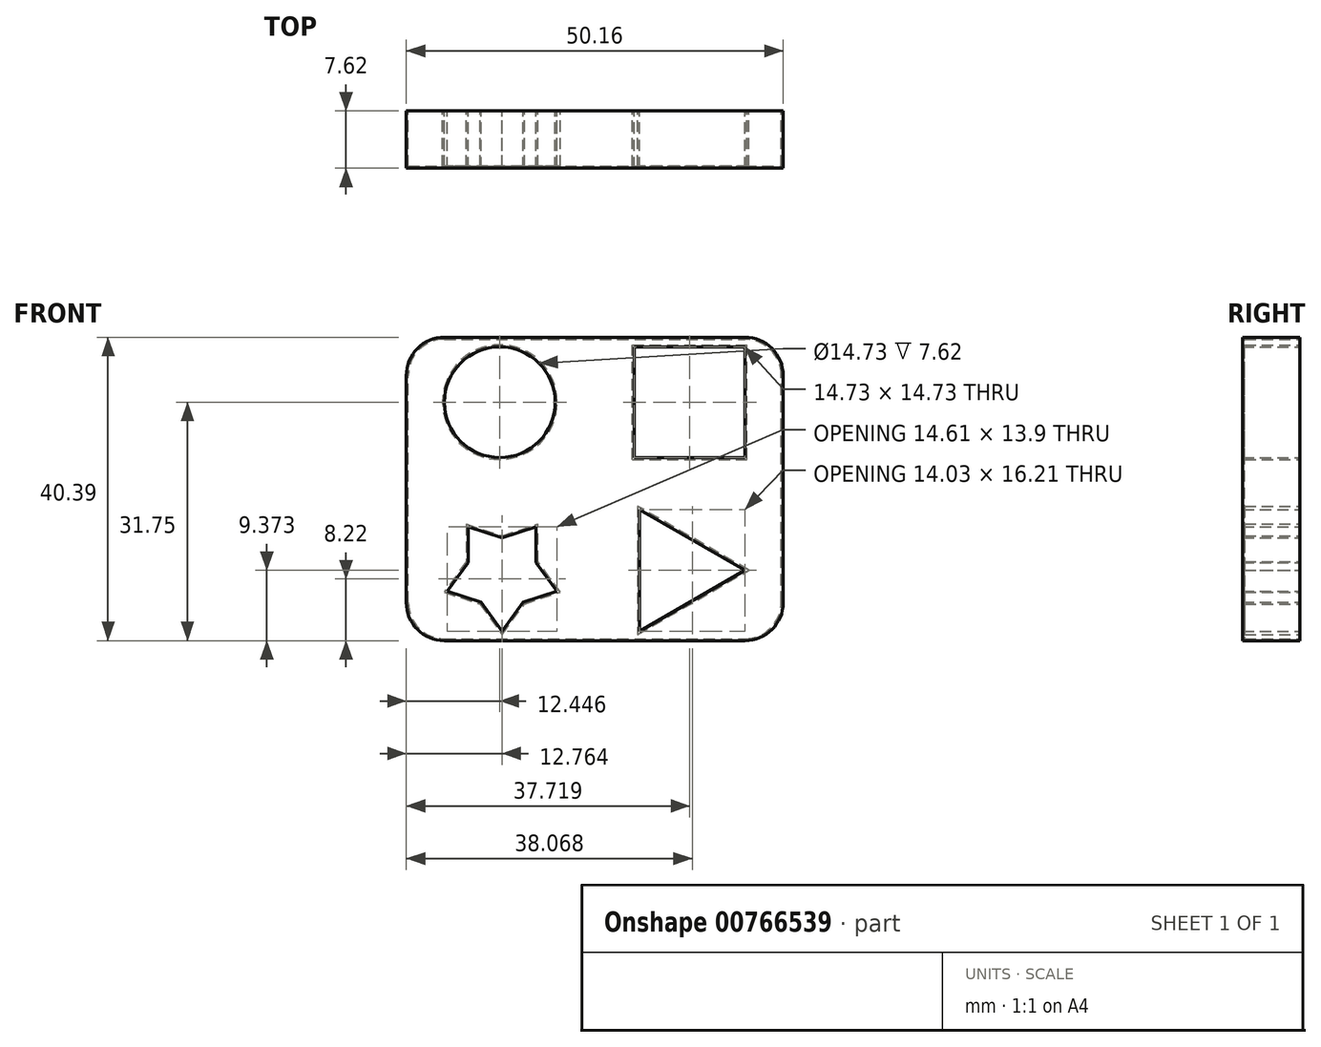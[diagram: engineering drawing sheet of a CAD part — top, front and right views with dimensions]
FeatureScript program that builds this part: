
annotation { "Feature Type Name" : "Feature", "Feature Type Description" : "" }
export const myFeature = defineFeature(function(context is Context, id is Id, definition is map)
    precondition{}
    {
        {
            var Q0;
            Q0=qCreatedBy(makeId("Front.planeOp"),FACE);
            var sketch = newSketch(context, id + "F0", { "sketchPlane" : qUnion([Q0])});
            skLineSegment(sketch, "E0.bottom", {"start": v(5.08, 0) * mm, "end": v(45.08, 0) * mm});
            skLineSegment(sketch, "E0.top", {"start": v(5.08, 40.39) * mm, "end": v(45.09, 40.39) * mm});
            skLineSegment(sketch, "E0.left", {"start": v(0, 5.08) * mm, "end": v(0, 35.3) * mm});
            skLineSegment(sketch, "E0.right", {"start": v(50.16, 5.08) * mm, "end": v(50.16, 35.3) * mm});
            skPoint(sketch, "E1.visualSharp", {"position": v(0, 40.39) * mm});
            skArc(sketch, "E1.filletArc", {"start": v(5.08, 40.39) * mm, "mid": v(1.49, 38.9) * mm, "end": v(0, 35.3) * mm});
            skPoint(sketch, "E2.visualSharp", {"position": v(0, 0) * mm});
            skArc(sketch, "E2.filletArc", {"start": v(0, 5.08) * mm, "mid": v(1.49, 1.49) * mm, "end": v(5.08, 0) * mm});
            skPoint(sketch, "E3.visualSharp", {"position": v(50.16, 0) * mm});
            skArc(sketch, "E3.filletArc", {"start": v(45.09, 0) * mm, "mid": v(48.68, 1.49) * mm, "end": v(50.17, 5.08) * mm});
            skPoint(sketch, "E4.visualSharp", {"position": v(50.17, 40.39) * mm});
            skArc(sketch, "E4.filletArc", {"start": v(50.17, 35.3) * mm, "mid": v(48.68, 38.9) * mm, "end": v(45.09, 40.39) * mm});
            skLineSegment(sketch, "E5.bottom", {"start": v(30.35, 24.38) * mm, "end": v(45.09, 24.38) * mm});
            skLineSegment(sketch, "E5.top", {"start": v(30.35, 39.12) * mm, "end": v(45.09, 39.12) * mm});
            skLineSegment(sketch, "E5.left", {"start": v(30.35, 24.38) * mm, "end": v(30.35, 39.12) * mm});
            skLineSegment(sketch, "E5.right", {"start": v(45.08, 24.38) * mm, "end": v(45.08, 39.12) * mm});
            skCircle(sketch, "E6", {"center": v(12.45, 31.75) * mm, "radius": 7.37 * mm});
            skCircle(sketch, "E7.cCircle", {"center": v(12.76, 8.95) * mm, "radius": 7.68 * mm, "construction": true});
            skLineSegment(sketch, "E7.0", {"start": v(17.28, 15.17) * mm, "end": v(20.07, 6.58) * mm, "construction": true});
            skLineSegment(sketch, "E7.1", {"start": v(20.07, 6.58) * mm, "end": v(12.76, 1.27) * mm, "construction": true});
            skLineSegment(sketch, "E7.2", {"start": v(12.76, 1.27) * mm, "end": v(5.46, 6.58) * mm, "construction": true});
            skLineSegment(sketch, "E7.3", {"start": v(5.46, 6.58) * mm, "end": v(8.25, 15.17) * mm, "construction": true});
            skLineSegment(sketch, "E7.4", {"start": v(8.25, 15.17) * mm, "end": v(17.28, 15.17) * mm, "construction": true});
            skLineSegment(sketch, "E8", {"start": v(8.25, 15.17) * mm, "end": v(12.76, 13.7) * mm});
            skLineSegment(sketch, "E9", {"start": v(12.76, 13.7) * mm, "end": v(17.28, 15.17) * mm});
            skLineSegment(sketch, "E10", {"start": v(16.42, 3.92) * mm, "end": v(12.76, 8.95) * mm, "construction": true});
            skLineSegment(sketch, "E11", {"start": v(9.1, 3.92) * mm, "end": v(12.76, 8.95) * mm, "construction": true});
            skLineSegment(sketch, "E12", {"start": v(18.68, 10.87) * mm, "end": v(12.76, 8.95) * mm, "construction": true});
            skLineSegment(sketch, "E13", {"start": v(6.85, 10.87) * mm, "end": v(12.76, 8.95) * mm, "construction": true});
            skLineSegment(sketch, "E14", {"start": v(8.25, 15.17) * mm, "end": v(8.25, 10.42) * mm});
            skLineSegment(sketch, "E15", {"start": v(8.25, 10.42) * mm, "end": v(5.46, 6.58) * mm});
            skLineSegment(sketch, "E16", {"start": v(5.46, 6.58) * mm, "end": v(9.97, 5.11) * mm});
            skLineSegment(sketch, "E17", {"start": v(9.97, 5.11) * mm, "end": v(12.76, 1.27) * mm});
            skLineSegment(sketch, "E18", {"start": v(12.76, 1.27) * mm, "end": v(15.55, 5.11) * mm});
            skLineSegment(sketch, "E19", {"start": v(15.55, 5.11) * mm, "end": v(20.07, 6.58) * mm});
            skLineSegment(sketch, "E20", {"start": v(20.07, 6.58) * mm, "end": v(17.28, 10.42) * mm});
            skLineSegment(sketch, "E21", {"start": v(17.28, 10.42) * mm, "end": v(17.28, 15.17) * mm});
            skLineSegment(sketch, "E22", {"start": v(31.05, 17.48) * mm, "end": v(31.05, 1.27) * mm});
            skLineSegment(sketch, "E23", {"start": v(31.05, 1.27) * mm, "end": v(45.09, 9.37) * mm});
            skLineSegment(sketch, "E24", {"start": v(45.09, 9.37) * mm, "end": v(31.05, 17.48) * mm});
            skSolve(sketch);
        }
        {
            var Q0;
            Q0=makeQuery(id+"F0.imprint","IMPRINT",FACE,{"disambiguationData":[TD([[makeQuery(id+"F0.imprint","IMPRINT",EDGE,{"derivedFrom":sQuery(id+"F0.wireOp",EDGE,"E0.bottom")}),1.0]])]});
            extrude(context, id + "F1", {"entities" : qUnion([Q0]), "depth" : 7.62 * mm, "offsetDistance" : 25.4 * mm});
        }
        {
            var Q0;
            Q0=makeQuery(id+"F1.opExtrude","CAP_FACE",FACE,{"disambiguationData":[OSD([sQuery(id+"F0.wireOp",EDGE,"E0.bottom"),sQuery(id+"F0.wireOp",EDGE,"E0.top"),sQuery(id+"F0.wireOp",EDGE,"E0.left"),sQuery(id+"F0.wireOp",EDGE,"E0.right"),sQuery(id+"F0.wireOp",EDGE,"E1.filletArc"),sQuery(id+"F0.wireOp",EDGE,"E2.filletArc"),sQuery(id+"F0.wireOp",EDGE,"E3.filletArc"),sQuery(id+"F0.wireOp",EDGE,"E4.filletArc"),sQuery(id+"F0.wireOp",EDGE,"E5.bottom"),sQuery(id+"F0.wireOp",EDGE,"E5.top"),sQuery(id+"F0.wireOp",EDGE,"E5.left"),sQuery(id+"F0.wireOp",EDGE,"E5.right"),sQuery(id+"F0.wireOp",EDGE,"E6"),sQuery(id+"F0.wireOp",EDGE,"E8"),sQuery(id+"F0.wireOp",EDGE,"E9"),sQuery(id+"F0.wireOp",EDGE,"E14"),sQuery(id+"F0.wireOp",EDGE,"E15"),sQuery(id+"F0.wireOp",EDGE,"E16"),sQuery(id+"F0.wireOp",EDGE,"E17"),sQuery(id+"F0.wireOp",EDGE,"E18"),sQuery(id+"F0.wireOp",EDGE,"E19"),sQuery(id+"F0.wireOp",EDGE,"E20"),sQuery(id+"F0.wireOp",EDGE,"E21"),sQuery(id+"F0.wireOp",EDGE,"E22"),sQuery(id+"F0.wireOp",EDGE,"E23"),sQuery(id+"F0.wireOp",EDGE,"E24")])],"isStart":true});
            shell(context, id + "F2", {"entities" : qUnion([Q0]), "thickness" : 0.25 * mm});
        }
    });
